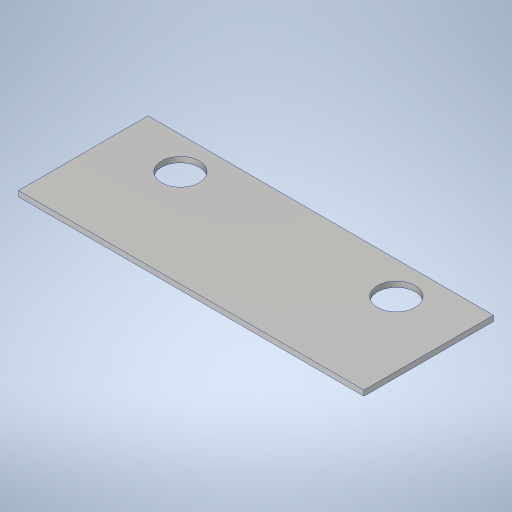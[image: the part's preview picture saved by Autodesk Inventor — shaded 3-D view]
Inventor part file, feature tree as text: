
AUTODESK INVENTOR PART (.ipt)
format: ipt  version: 2023.4 (Build 274418000, 418)  size: 231,424 bytes
history: native  units: in
note: dims shown in document units (in); Inventor stores cm internally (conversion verified against a paired STEP export)
features: sketch x2, extrude x1, hole x1
ambient origin geometry x8: Origin, YZ Plane, XZ Plane, XY Plane, X Axis, Y Axis, Z Axis, Center Point
bodies: Solid1 (feature_tree)
feature tree (4):
  extrude  "Extrusion1"  Depth=3.0in
  hole  "Hole1"  [1 undecoded]
  sketch  "Sketch1"  dims[d0=8.0in d1=3.0in]
  sketch  "Sketch2"  dims[d2=0.125in d3=0.0in d4=0.75in d5=2.5in d6=0.875in d7=0.75in d8=0.375in d9=0.25in d10=0.5635in d11=1.0in d12=0.8108in]
note: 1 required parameter value undecoded (feature->parameter linkage not recoverable at this tier; creation-order binding heuristic only, values carry confidence <= 0.55)
